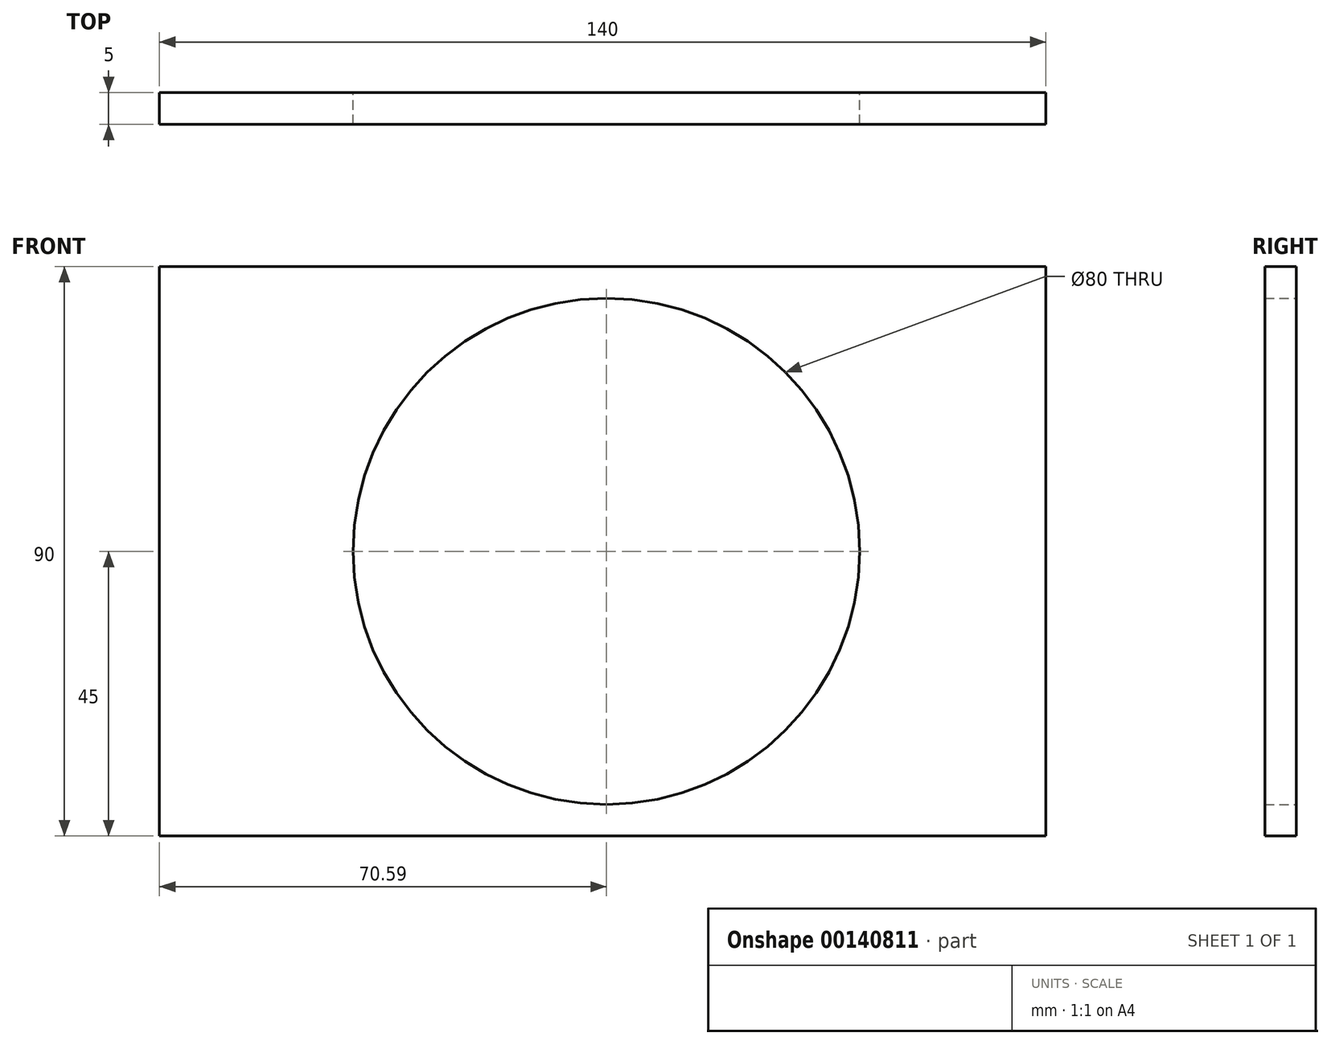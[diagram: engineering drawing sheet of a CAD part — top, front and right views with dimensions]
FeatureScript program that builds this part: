
annotation { "Feature Type Name" : "Feature", "Feature Type Description" : "" }
export const myFeature = defineFeature(function(context is Context, id is Id, definition is map)
    precondition{}
    {
        {
            var Q0;
            Q0=qCreatedBy(makeId("Front.planeOp"),FACE);
            var sketch = newSketch(context, id + "F0", { "sketchPlane" : qUnion([Q0])});
            skCircle(sketch, "E0", {"center": v(0, 0) * mm, "radius": 40 * mm});
            skLineSegment(sketch, "E1", {"start": v(0, 0) * mm, "end": v(70, 0) * mm});
            skLineSegment(sketch, "E2.MirrorCS", {"start": v(0, 0) * mm, "end": v(-70, 0) * mm});
            skLineSegment(sketch, "E3", {"start": v(-70.6, 45) * mm, "end": v(69.4, 45) * mm});
            skLineSegment(sketch, "E4.MirrorCS", {"start": v(-70.6, -45) * mm, "end": v(69.4, -45) * mm});
            skLineSegment(sketch, "E5", {"start": v(-70.6, 45) * mm, "end": v(-70.6, -45) * mm});
            skLineSegment(sketch, "E6", {"start": v(69.4, 45) * mm, "end": v(69.4, -45) * mm});
            skSolve(sketch);
        }
        {
            var Q0;
            Q0 = qSketchRegion(id + "F0", true);
            extrude(context, id + "F1", {"entities" : qUnion([Q0]), "depth" : 5 * mm});
        }
    });
